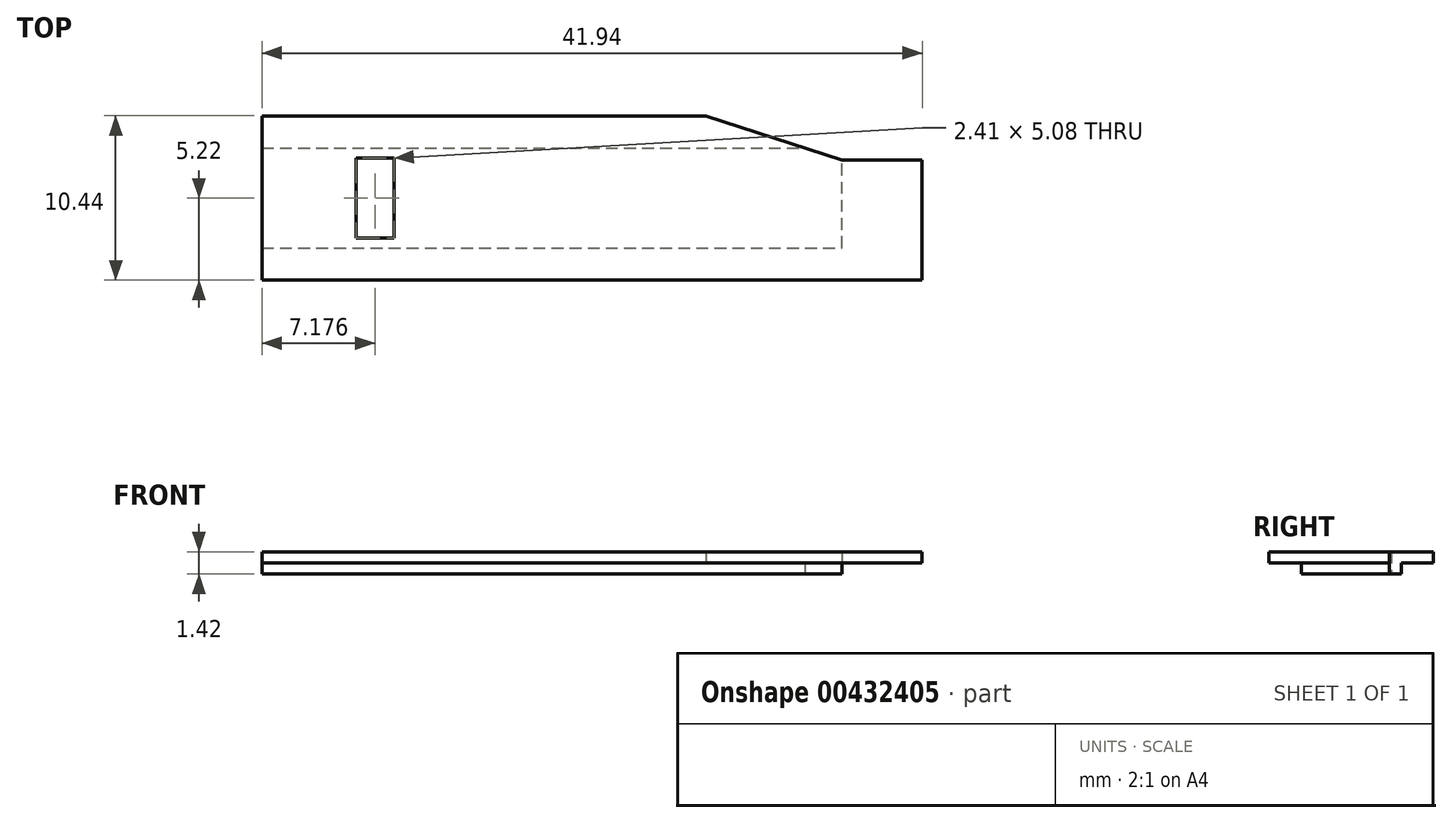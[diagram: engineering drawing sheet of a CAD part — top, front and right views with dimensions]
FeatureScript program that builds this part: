
annotation { "Feature Type Name" : "Feature", "Feature Type Description" : "" }
export const myFeature = defineFeature(function(context is Context, id is Id, definition is map)
    precondition{}
    {
        {
            var Q0;
            Q0=qCreatedBy(makeId("Top.planeOp"),FACE);
            var sketch = newSketch(context, id + "F0", { "sketchPlane" : qUnion([Q0])});
            skLineSegment(sketch, "E0.bottom", {"start": v(0, 0) * mm, "end": v(28.2, 0) * mm});
            skLineSegment(sketch, "E0.top", {"start": v(0, 10.44) * mm, "end": v(28.2, 10.44) * mm});
            skLineSegment(sketch, "E0.left", {"start": v(0, 0) * mm, "end": v(0, 10.44) * mm});
            skLineSegment(sketch, "E0.right", {"start": v(28.2, 0) * mm, "end": v(28.2, 10.44) * mm});
            skLineSegment(sketch, "E1.bottom", {"start": v(36.86, 0) * mm, "end": v(41.94, 0) * mm});
            skLineSegment(sketch, "E1.top", {"start": v(36.86, 7.65) * mm, "end": v(41.94, 7.65) * mm});
            skLineSegment(sketch, "E1.left", {"start": v(36.86, 0) * mm, "end": v(36.86, 7.65) * mm});
            skLineSegment(sketch, "E1.right", {"start": v(41.94, 0) * mm, "end": v(41.94, 7.65) * mm});
            skLineSegment(sketch, "E2", {"start": v(28.2, 10.44) * mm, "end": v(36.86, 7.65) * mm});
            skLineSegment(sketch, "E3", {"start": v(28.2, 0) * mm, "end": v(36.86, 0) * mm});
            skLineSegment(sketch, "E4.bottom", {"start": v(8.38, 2.68) * mm, "end": v(5.97, 2.68) * mm});
            skLineSegment(sketch, "E4.top", {"start": v(8.38, 7.76) * mm, "end": v(5.97, 7.76) * mm});
            skLineSegment(sketch, "E4.left", {"start": v(8.38, 2.68) * mm, "end": v(8.38, 7.76) * mm});
            skLineSegment(sketch, "E4.right", {"start": v(5.97, 2.68) * mm, "end": v(5.97, 7.76) * mm});
            skPoint(sketch, "E4.middle", {"position": v(7.18, 5.22) * mm});
            skPoint(sketch, "E4.middle.positionSnap0", {"position": v(0, 5.22) * mm});
            skPoint(sketch, "E4.centerSnap0", {"position": v(0, 5.22) * mm});
            skSolve(sketch);
        }
        {
            var Q0;
            Q0 = qSketchRegion(id + "F0", true);
            extrude(context, id + "F1", {"entities" : qUnion([Q0]), "depth" : 0.71 * mm});
        }
        {
            var Q0;
            Q0=makeQuery(id+"F1.opExtrude","CAP_FACE",FACE,{"disambiguationData":[OSD([sQuery(id+"F0.wireOp",EDGE,"E0.bottom"),sQuery(id+"F0.wireOp",EDGE,"E0.top"),sQuery(id+"F0.wireOp",EDGE,"E0.left"),sQuery(id+"F0.wireOp",EDGE,"E1.bottom"),sQuery(id+"F0.wireOp",EDGE,"E1.top"),sQuery(id+"F0.wireOp",EDGE,"E1.right"),sQuery(id+"F0.wireOp",EDGE,"E2"),sQuery(id+"F0.wireOp",EDGE,"E3"),sQuery(id+"F0.wireOp",EDGE,"E4.bottom"),sQuery(id+"F0.wireOp",EDGE,"E4.top"),sQuery(id+"F0.wireOp",EDGE,"E4.left"),sQuery(id+"F0.wireOp",EDGE,"E4.right")])],"isStart":true});
            var sketch = newSketch(context, id + "F2", { "sketchPlane" : qUnion([Q0])});
            skLineSegment(sketch, "E5", {"start": v(0, -5.22) * mm, "end": v(41.94, -5.22) * mm, "construction": true});
            skLineSegment(sketch, "E6.bottom", {"start": v(0, -2.04) * mm, "end": v(36.86, -2.04) * mm});
            skLineSegment(sketch, "E6.top", {"start": v(0, -8.4) * mm, "end": v(36.86, -8.4) * mm});
            skLineSegment(sketch, "E6.left", {"start": v(0, -2.04) * mm, "end": v(0, -8.4) * mm});
            skLineSegment(sketch, "E6.right", {"start": v(36.86, -2.04) * mm, "end": v(36.86, -8.4) * mm});
            skLineSegment(sketch, "E7.0", {"start": v(5.97, -2.68) * mm, "end": v(5.97, -7.76) * mm});
            skLineSegment(sketch, "E8.0", {"start": v(8.38, -2.68) * mm, "end": v(5.97, -2.68) * mm});
            skLineSegment(sketch, "E9.0", {"start": v(8.38, -2.68) * mm, "end": v(8.38, -7.76) * mm});
            skLineSegment(sketch, "E10.0", {"start": v(8.38, -7.76) * mm, "end": v(5.97, -7.76) * mm});
            skSolve(sketch);
        }
        {
            var Q0;
            {var subQ3=sQuery(id+"F2.wireOp",EDGE,"E6.bottom");Q0=makeQuery(id+"F2.imprint","IMPRINT",FACE,{"disambiguationData":[TD([[makeQuery(id+"F2.imprint","IMPRINT",EDGE,{"derivedFrom":subQ3}),-1.0]])]});}
            extrude(context, id + "F3", {"entities" : qUnion([Q0]), "operationType" : NewBodyOperationType.ADD, "depth" : 0.71 * mm});
        }
    });
